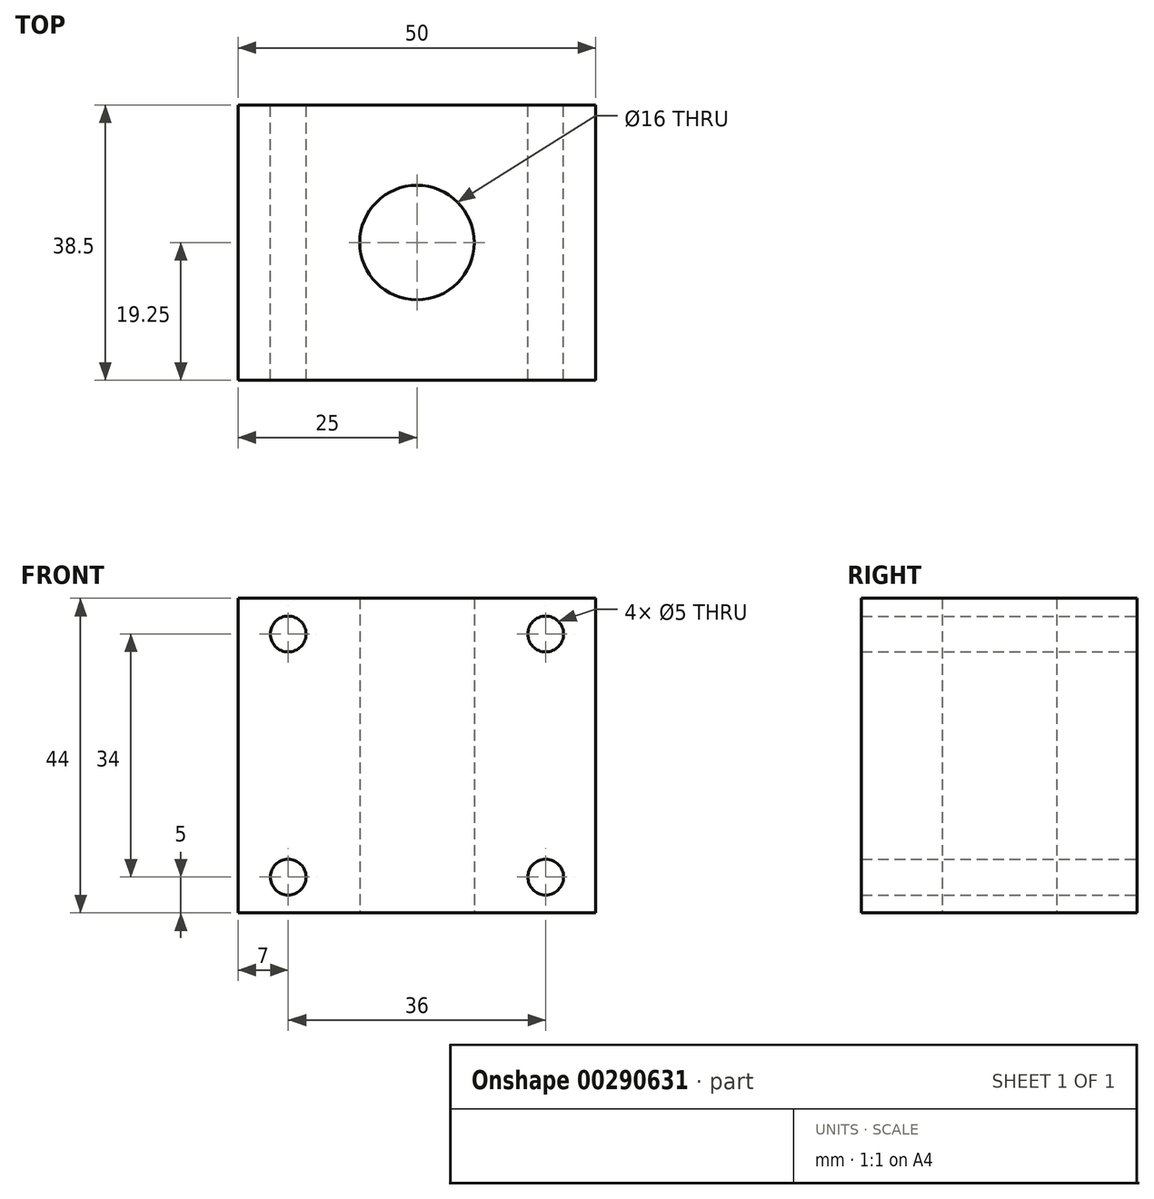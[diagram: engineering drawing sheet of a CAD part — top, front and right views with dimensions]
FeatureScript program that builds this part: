
annotation { "Feature Type Name" : "Feature", "Feature Type Description" : "" }
export const myFeature = defineFeature(function(context is Context, id is Id, definition is map)
    precondition{}
    {
        {
            var Q0;
            Q0=qCreatedBy(makeId("Top.planeOp"),FACE);
            var sketch = newSketch(context, id + "F0", { "sketchPlane" : qUnion([Q0])});
            skLineSegment(sketch, "E0.bottom", {"start": v(-25, 19.25) * mm, "end": v(25, 19.25) * mm});
            skLineSegment(sketch, "E0.top", {"start": v(-25, -19.25) * mm, "end": v(25, -19.25) * mm});
            skLineSegment(sketch, "E0.left", {"start": v(-25, 19.25) * mm, "end": v(-25, -19.25) * mm});
            skLineSegment(sketch, "E0.right", {"start": v(25, 19.25) * mm, "end": v(25, -19.25) * mm});
            skLineSegment(sketch, "E1", {"start": v(0, 19.25) * mm, "end": v(0, -19.25) * mm, "construction": true});
            skLineSegment(sketch, "E2", {"start": v(-25, 0) * mm, "end": v(25, 0) * mm, "construction": true});
            skCircle(sketch, "E3", {"center": v(0, 0) * mm, "radius": 8 * mm});
            skSolve(sketch);
        }
        {
            var Q0;
            Q0 = qSketchRegion(id + "F0", true);
            extrude(context, id + "F1", {"entities" : qUnion([Q0]), "depth" : 44 * mm});
        }
        {
            var Q0;
            Q0=makeQuery(id+"F1.opExtrude","SWEPT_FACE",FACE,{"disambiguationData":[OSD([sQuery(id+"F0.wireOp",EDGE,"E0.bottom")])]});
            var sketch = newSketch(context, id + "F2", { "sketchPlane" : qUnion([Q0])});
            skLineSegment(sketch, "E4", {"start": v(0, 44) * mm, "end": v(0, 0) * mm, "construction": true});
            skLineSegment(sketch, "E5", {"start": v(-25, 22) * mm, "end": v(25, 22) * mm, "construction": true});
            skCircle(sketch, "E6", {"center": v(18, 39) * mm, "radius": 2.5 * mm});
            skCircle(sketch, "E7", {"center": v(18, 5) * mm, "radius": 2.5 * mm});
            skCircle(sketch, "E8.MirrorC", {"center": v(-18, 39) * mm, "radius": 2.5 * mm});
            skCircle(sketch, "E9.MirrorC", {"center": v(-18, 5) * mm, "radius": 2.5 * mm});
            skSolve(sketch);
        }
        {
            var Q0;
            Q0 = qSketchRegion(id + "F2", true);
            extrude(context, id + "F3", {"entities" : qUnion([Q0]), "operationType" : NewBodyOperationType.REMOVE, "oppositeDirection" : true, "depth" : 38.5 * mm});
        }
    });
